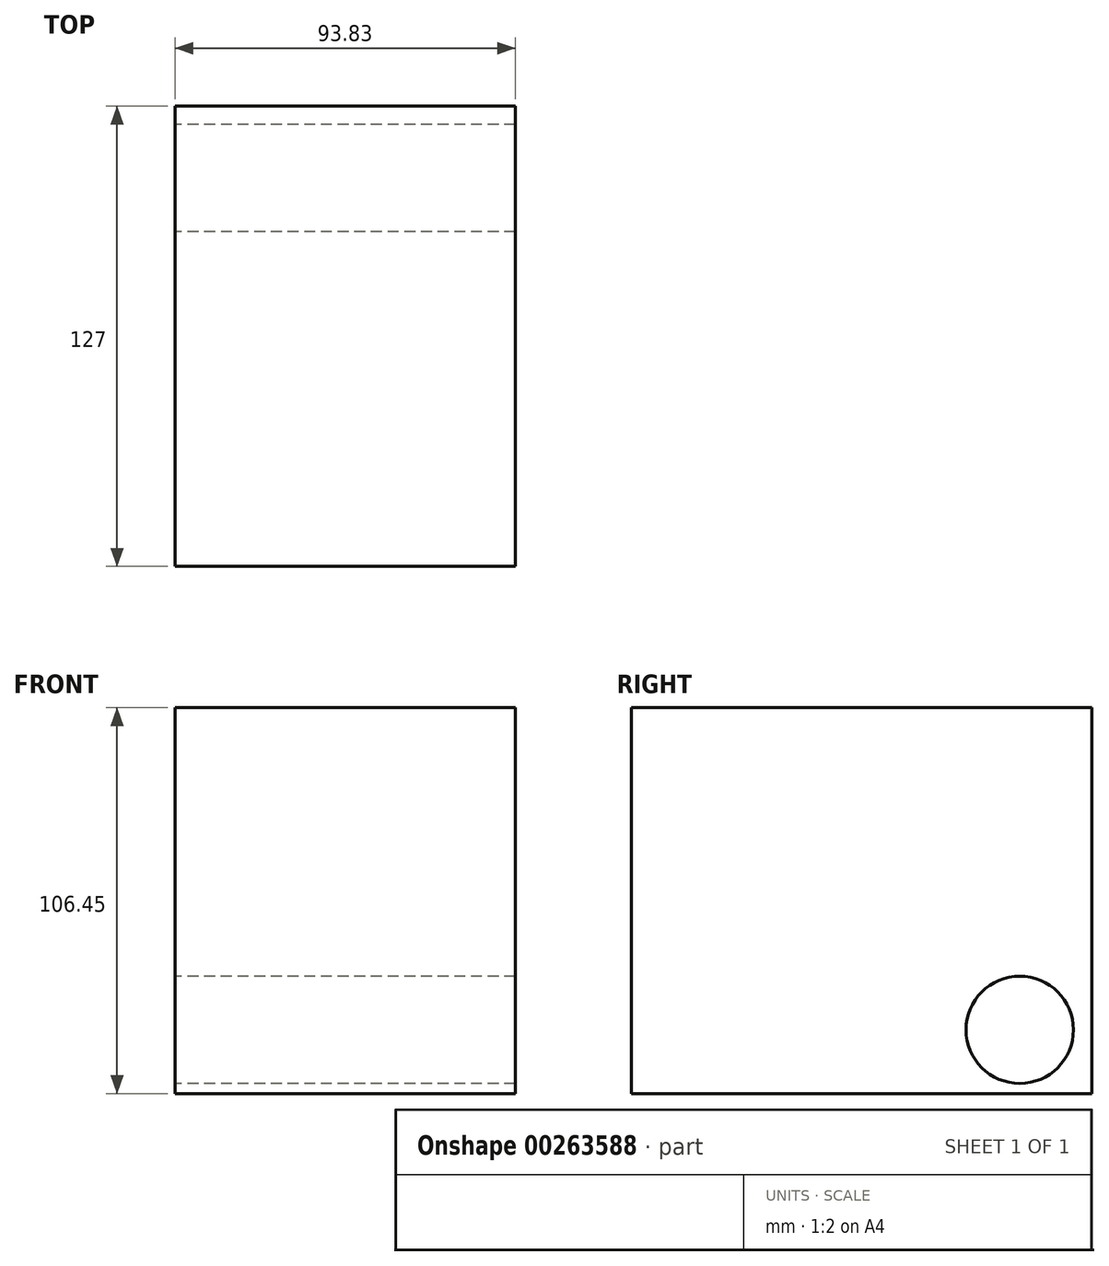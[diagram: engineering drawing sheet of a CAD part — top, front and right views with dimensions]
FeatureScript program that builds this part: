
annotation { "Feature Type Name" : "Feature", "Feature Type Description" : "" }
export const myFeature = defineFeature(function(context is Context, id is Id, definition is map)
    precondition{}
    {
        {
            var Q0;
            Q0=qCreatedBy(makeId("Front.planeOp"),FACE);
            var sketch = newSketch(context, id + "F0", { "sketchPlane" : qUnion([Q0])});
            skLineSegment(sketch, "E0.bottom", {"start": v(0, 0) * mm, "end": v(-93.83, 0) * mm});
            skLineSegment(sketch, "E0.top", {"start": v(0, 106.45) * mm, "end": v(-93.83, 106.45) * mm});
            skLineSegment(sketch, "E0.left", {"start": v(0, 0) * mm, "end": v(0, 106.45) * mm});
            skLineSegment(sketch, "E0.right", {"start": v(-93.83, 0) * mm, "end": v(-93.83, 106.45) * mm});
            skSolve(sketch);
        }
        {
            var Q0;
            Q0=makeQuery(id+"F0.imprint","IMPRINT",FACE,{"disambiguationData":[TD([[makeQuery(id+"F0.imprint","IMPRINT",EDGE,{"derivedFrom":sQuery(id+"F0.wireOp",EDGE,"E0.bottom")}),-1.0]])]});
            extrude(context, id + "F1", {"entities" : qUnion([Q0]), "depth" : 127 * mm});
        }
        {
            var Q0;
            Q0=makeQuery(id+"F1.opExtrude","SWEPT_FACE",FACE,{"disambiguationData":[OSD([sQuery(id+"F0.wireOp",EDGE,"E0.right")])]});
            var sketch = newSketch(context, id + "F2", { "sketchPlane" : qUnion([Q0])});
            skCircle(sketch, "E1", {"center": v(19.86, 17.58) * mm, "radius": 14.8 * mm});
            skSolve(sketch);
        }
        {
            var Q0;
            Q0=makeQuery(id+"F2.imprint","IMPRINT",FACE,{"disambiguationData":[TD([[makeQuery(id+"F2.imprint","IMPRINT",EDGE,{"derivedFrom":sQuery(id+"F2.wireOp",EDGE,"E1")}),1.0]])]});
            extrude(context, id + "F3", {"entities" : qUnion([Q0]), "operationType" : NewBodyOperationType.REMOVE, "endBound" : BoundingType.UP_TO_NEXT, "oppositeDirection" : true, "depth" : 25.4 * mm});
        }
    });
